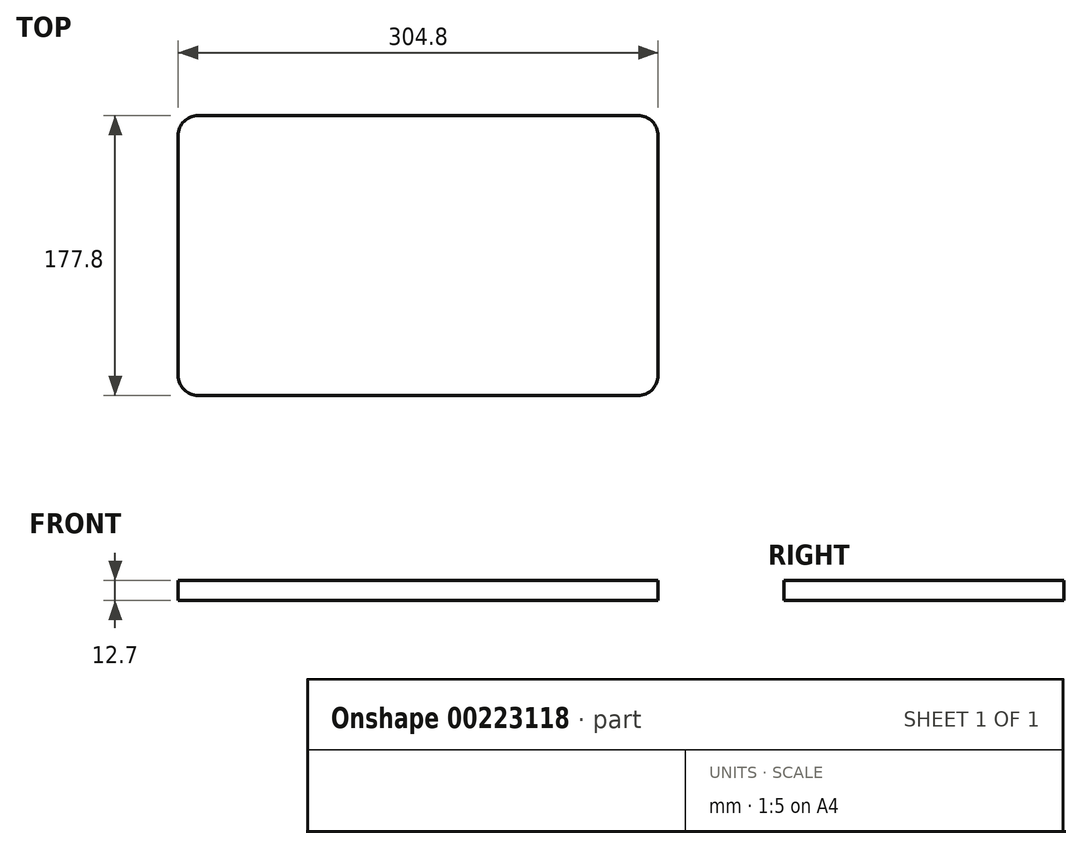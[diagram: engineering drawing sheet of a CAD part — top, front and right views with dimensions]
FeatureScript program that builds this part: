
annotation { "Feature Type Name" : "Feature", "Feature Type Description" : "" }
export const myFeature = defineFeature(function(context is Context, id is Id, definition is map)
    precondition{}
    {
        {
            var Q0;
            Q0=qCreatedBy(makeId("Top.planeOp"),FACE);
            var sketch = newSketch(context, id + "F0", { "sketchPlane" : qUnion([Q0])});
            skLineSegment(sketch, "E0.bottom", {"start": v(-152.4, 88.9) * mm, "end": v(152.4, 88.9) * mm});
            skLineSegment(sketch, "E0.top", {"start": v(-152.4, -88.9) * mm, "end": v(152.4, -88.9) * mm});
            skLineSegment(sketch, "E0.left", {"start": v(-152.4, 88.9) * mm, "end": v(-152.4, -88.9) * mm});
            skLineSegment(sketch, "E0.right", {"start": v(152.4, 88.9) * mm, "end": v(152.4, -88.9) * mm});
            skPoint(sketch, "E0.middle", {"position": v(0, 0) * mm});
            skLineSegment(sketch, "E1.bottom", {"start": v(-139.7, -76.2) * mm, "end": v(139.7, -76.2) * mm});
            skLineSegment(sketch, "E1.top", {"start": v(-139.7, 76.2) * mm, "end": v(139.7, 76.2) * mm});
            skLineSegment(sketch, "E1.left", {"start": v(-139.7, -76.2) * mm, "end": v(-139.7, 76.2) * mm});
            skLineSegment(sketch, "E1.right", {"start": v(139.7, -76.2) * mm, "end": v(139.7, 76.2) * mm});
            skCircle(sketch, "E2", {"center": v(-139.7, -76.2) * mm, "radius": 12.7 * mm});
            skCircle(sketch, "E3", {"center": v(139.7, -76.2) * mm, "radius": 12.7 * mm});
            skCircle(sketch, "E4", {"center": v(139.7, 76.2) * mm, "radius": 12.7 * mm});
            skCircle(sketch, "E5", {"center": v(-139.7, 76.2) * mm, "radius": 12.7 * mm});
            skSolve(sketch);
        }
        {
            var Q0;
            {var subQ0=sQuery(id+"F0.wireOp",EDGE,"E5");var subQ1=sQuery(id+"F0.wireOp",EDGE,"E0.left");var subQ2=makeQuery(id+"F0.imprint","INTERSECT",VERTEX,{"derivedFrom":[subQ1,subQ0]});Q0=makeQuery(id+"F0.imprint","IMPRINT",FACE,{"disambiguationData":[TD([[makeQuery(id+"F0.imprint","IMPRINT",EDGE,{"disambiguationData":[TD([[subQ2,-1.0]])],"derivedFrom":subQ1}),1.0]])]});}
            var Q1;
            {var subQ3=sQuery(id+"F0.wireOp",EDGE,"E1.left");var subQ5=sQuery(id+"F0.wireOp",EDGE,"E1.bottom");var subQ6=makeQuery(id+"F0.imprint","INTERSECT",VERTEX,{"derivedFrom":[subQ5,subQ3]});Q1=makeQuery(id+"F0.imprint","IMPRINT",FACE,{"disambiguationData":[TD([[makeQuery(id+"F0.imprint","IMPRINT",EDGE,{"disambiguationData":[TD([[subQ6,-1.0]])],"derivedFrom":subQ5}),-1.0]])]});}
            var Q2;
            {var subQ5=sQuery(id+"F0.wireOp",EDGE,"E1.bottom");var subQ7=sQuery(id+"F0.wireOp",EDGE,"E2");var subQ15=makeQuery(id+"F0.imprint","INTERSECT",VERTEX,{"derivedFrom":[subQ5,subQ7]});Q2=makeQuery(id+"F0.imprint","IMPRINT",FACE,{"disambiguationData":[TD([[makeQuery(id+"F0.imprint","IMPRINT",EDGE,{"disambiguationData":[TD([[subQ15,-1.0]])],"derivedFrom":subQ5}),1.0]])]});}
            var Q3;
            {var subQ3=sQuery(id+"F0.wireOp",EDGE,"E1.left");var subQ5=sQuery(id+"F0.wireOp",EDGE,"E1.top");var subQ7=makeQuery(id+"F0.imprint","INTERSECT",VERTEX,{"derivedFrom":[subQ5,subQ3]});Q3=makeQuery(id+"F0.imprint","IMPRINT",FACE,{"disambiguationData":[TD([[makeQuery(id+"F0.imprint","IMPRINT",EDGE,{"disambiguationData":[TD([[subQ7,-1.0]])],"derivedFrom":subQ5}),1.0]])]});}
            var Q4;
            {var subQ0=sQuery(id+"F0.wireOp",EDGE,"E1.left");var subQ1=sQuery(id+"F0.wireOp",EDGE,"E1.top");var subQ2=makeQuery(id+"F0.imprint","INTERSECT",VERTEX,{"derivedFrom":[subQ1,subQ0]});Q4=makeQuery(id+"F0.imprint","IMPRINT",FACE,{"disambiguationData":[TD([[makeQuery(id+"F0.imprint","IMPRINT",EDGE,{"disambiguationData":[TD([[subQ2,-1.0]])],"derivedFrom":subQ1}),-1.0]])]});}
            var Q5;
            {var subQ0=sQuery(id+"F0.wireOp",EDGE,"E5");var subQ1=sQuery(id+"F0.wireOp",EDGE,"E0.bottom");var subQ2=makeQuery(id+"F0.imprint","INTERSECT",VERTEX,{"derivedFrom":[subQ1,subQ0]});Q5=makeQuery(id+"F0.imprint","IMPRINT",FACE,{"disambiguationData":[TD([[makeQuery(id+"F0.imprint","IMPRINT",EDGE,{"disambiguationData":[TD([[subQ2,-1.0]])],"derivedFrom":subQ1}),-1.0]])]});}
            var Q6;
            {var subQ2=sQuery(id+"F0.wireOp",EDGE,"E1.top");var subQ4=sQuery(id+"F0.wireOp",EDGE,"E1.right");var subQ5=makeQuery(id+"F0.imprint","INTERSECT",VERTEX,{"derivedFrom":[subQ2,subQ4]});Q6=makeQuery(id+"F0.imprint","IMPRINT",FACE,{"disambiguationData":[TD([[makeQuery(id+"F0.imprint","IMPRINT",EDGE,{"disambiguationData":[TD([[subQ5,1.0]])],"derivedFrom":subQ2}),1.0]])]});}
            var Q7;
            {var subQ0=sQuery(id+"F0.wireOp",EDGE,"E1.right");var subQ1=sQuery(id+"F0.wireOp",EDGE,"E1.top");var subQ2=makeQuery(id+"F0.imprint","INTERSECT",VERTEX,{"derivedFrom":[subQ1,subQ0]});Q7=makeQuery(id+"F0.imprint","IMPRINT",FACE,{"disambiguationData":[TD([[makeQuery(id+"F0.imprint","IMPRINT",EDGE,{"disambiguationData":[TD([[subQ2,1.0]])],"derivedFrom":subQ1}),-1.0]])]});}
            var Q8;
            {var subQ0=sQuery(id+"F0.wireOp",EDGE,"E4");var subQ1=sQuery(id+"F0.wireOp",EDGE,"E0.right");var subQ2=makeQuery(id+"F0.imprint","INTERSECT",VERTEX,{"derivedFrom":[subQ1,subQ0]});Q8=makeQuery(id+"F0.imprint","IMPRINT",FACE,{"disambiguationData":[TD([[makeQuery(id+"F0.imprint","IMPRINT",EDGE,{"disambiguationData":[TD([[subQ2,-1.0]])],"derivedFrom":subQ1}),-1.0]])]});}
            var Q9;
            {var subQ0=sQuery(id+"F0.wireOp",EDGE,"E1.right");var subQ1=sQuery(id+"F0.wireOp",EDGE,"E1.bottom");var subQ2=makeQuery(id+"F0.imprint","INTERSECT",VERTEX,{"derivedFrom":[subQ1,subQ0]});Q9=makeQuery(id+"F0.imprint","IMPRINT",FACE,{"disambiguationData":[TD([[makeQuery(id+"F0.imprint","IMPRINT",EDGE,{"disambiguationData":[TD([[subQ2,1.0]])],"derivedFrom":subQ1}),1.0]])]});}
            var Q10;
            {var subQ0=sQuery(id+"F0.wireOp",EDGE,"E1.right");var subQ1=sQuery(id+"F0.wireOp",EDGE,"E1.bottom");var subQ2=makeQuery(id+"F0.imprint","INTERSECT",VERTEX,{"derivedFrom":[subQ1,subQ0]});Q10=makeQuery(id+"F0.imprint","IMPRINT",FACE,{"disambiguationData":[TD([[makeQuery(id+"F0.imprint","IMPRINT",EDGE,{"disambiguationData":[TD([[subQ2,1.0]])],"derivedFrom":subQ1}),-1.0]])]});}
            var Q11;
            {var subQ0=sQuery(id+"F0.wireOp",EDGE,"E2");var subQ1=sQuery(id+"F0.wireOp",EDGE,"E0.top");var subQ2=makeQuery(id+"F0.imprint","INTERSECT",VERTEX,{"derivedFrom":[subQ1,subQ0]});Q11=makeQuery(id+"F0.imprint","IMPRINT",FACE,{"disambiguationData":[TD([[makeQuery(id+"F0.imprint","IMPRINT",EDGE,{"disambiguationData":[TD([[subQ2,-1.0]])],"derivedFrom":subQ1}),1.0]])]});}
            var Q12;
            {var subQ0=sQuery(id+"F0.wireOp",EDGE,"E1.left");var subQ1=sQuery(id+"F0.wireOp",EDGE,"E1.bottom");var subQ2=makeQuery(id+"F0.imprint","INTERSECT",VERTEX,{"derivedFrom":[subQ1,subQ0]});Q12=makeQuery(id+"F0.imprint","IMPRINT",FACE,{"disambiguationData":[TD([[makeQuery(id+"F0.imprint","IMPRINT",EDGE,{"disambiguationData":[TD([[subQ2,-1.0]])],"derivedFrom":subQ1}),1.0]])]});}
            extrude(context, id + "F1", {"entities" : qUnion([Q0, Q1, Q2, Q3, Q4, Q5, Q6, Q7, Q8, Q9, Q10, Q11, Q12]), "depth" : 12.7 * mm});
        }
    });
